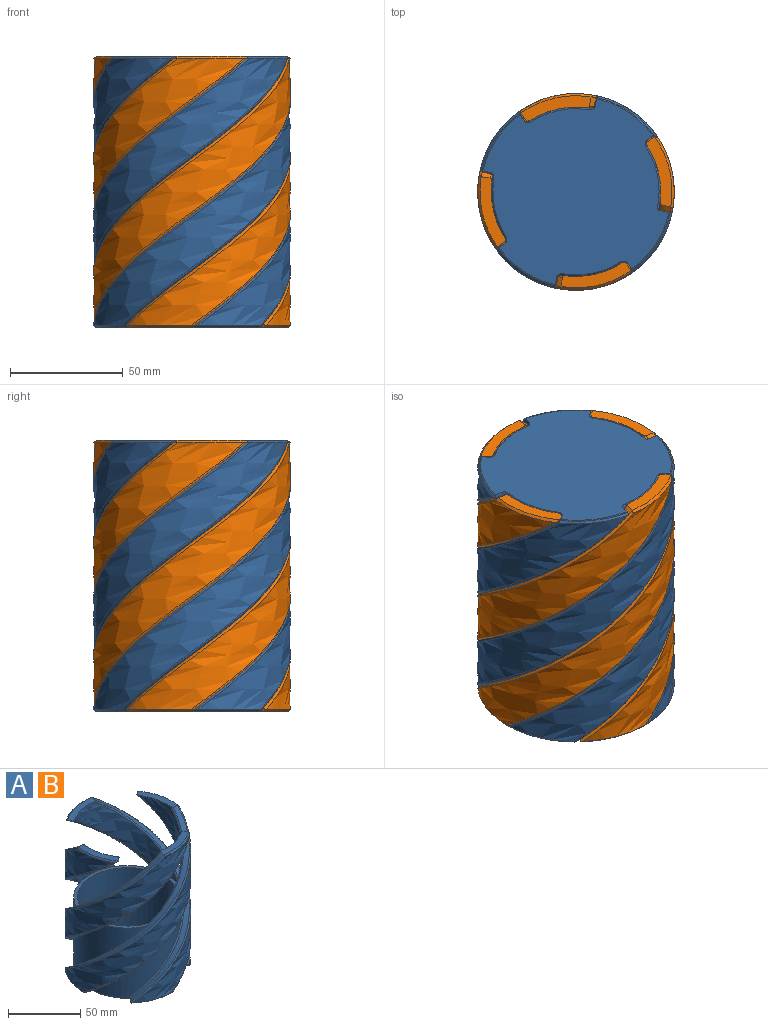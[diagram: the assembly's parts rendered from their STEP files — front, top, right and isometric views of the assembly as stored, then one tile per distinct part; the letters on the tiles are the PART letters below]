
ASSEMBLY  parts=2 mates=1
PART A: 91 faces, bbox 91.5x91.5x134.3 mm
  f0: cylinder r=37.5mm len=70.11mm, axis (0,0,-1), area 1564mm2, adj f4,f53,f57,f67
  f1: cylinder r=37.5mm len=70.11mm, axis (0,0,-1), area 1564mm2, adj f4,f56,f59,f68
  f2: cylinder r=37.5mm len=70.11mm, axis (0,0,-1), area 1564mm2, adj f4,f55,f58,f84
  f3: cylinder r=37.5mm len=70.84mm, axis (0,0,-1), area 1655.3mm2, adj f4,f16,f54,f83,f85
  f4: plane 75.41x75.41mm, normal (0,0,1), area 574.3mm2, adj f0,f1,f2,f3,f6,f10,f15,f16
  f5: plane 84.47x84.47mm, normal (0,0,-1), area 4878.4mm2, adj f62,f63,f64,f65,f66,f67,f68,f69
  f6: cylinder r=35mm len=70mm, axis (0,0,-1), area 11545.4mm2, adj f4,f52
  f7: plane 60x60mm, normal (0,0,1), area 2827.4mm2, adj f52
  f8: plane 32.05x12.18mm, normal (0,0,1), area 156.5mm2, adj f9,f10,f11,f33,f36,f50,f51
  f9: bspline ~130x87mm, area 776mm2, adj f8,f36,f50,f54,f79
  f10: bspline ~80x69.6mm, area 1583mm2, adj f4,f8,f50,f51
  f11: bspline ~130x88.08mm, area 768.6mm2, adj f8,f37,f51,f53,f71
  f12: bspline ~120x91.09mm, area 3627.8mm2, adj f31,f33,f36,f37
  f13: plane 32.05x12.18mm, normal (0,0,1), area 156.4mm2, adj f14,f15,f16,f32,f42,f48,f49
  f14: bspline ~130x87mm, area 776mm2, adj f13,f42,f48,f55,f89
  f15: bspline ~80x69.6mm, area 1583mm2, adj f4,f13,f48,f49
  f16: bspline ~130x88.08mm, area 859.5mm2, adj f3,f4,f13,f43,f49,f85
  f17: bspline ~120x91.09mm, area 3627.8mm2, adj f28,f32,f42,f43
  f18: plane 32.05x12.18mm, normal (0,0,1), area 156.3mm2, adj f20,f21,f22,f35,f41,f46,f47
  f19: bspline ~120x91.09mm, area 3627.8mm2, adj f29,f35,f40,f41
  f20: bspline ~130x87mm, area 776mm2, adj f18,f41,f46,f59,f74
  f21: bspline ~80x69.6mm, area 1583mm2, adj f4,f18,f46,f47
  f22: bspline ~130x88.08mm, area 768.6mm2, adj f18,f40,f47,f58,f80
  f23: plane 32.05x12.18mm, normal (0,0,1), area 157.8mm2, adj f25,f26,f27,f34,f39,f44,f45
  f24: bspline ~120x91.09mm, area 3627.8mm2, adj f30,f34,f38,f39
  f25: bspline ~130x87mm, area 776mm2, adj f23,f39,f44,f57,f63
  f26: bspline ~80x69.6mm, area 1583mm2, adj f4,f23,f44,f45
  f27: bspline ~130x88.08mm, area 768.6mm2, adj f23,f38,f45,f56,f64
  f28: bspline ~32.38x13.54mm, area 35.5mm2, adj f17,f42,f43,f86,f88
  f29: bspline ~32.38x13.54mm, area 35.5mm2, adj f19,f40,f41,f77,f78
  f30: bspline ~32.38x13.54mm, area 35.5mm2, adj f24,f38,f39,f61,f62
  f31: bspline ~32.38x13.54mm, area 35.5mm2, adj f12,f36,f37,f72,f75
  f32: bspline ~35.3x10.09mm, area 45.3mm2, adj f13,f17,f42,f43
  f33: bspline ~35.3x10.09mm, area 45.3mm2, adj f8,f12,f36,f37
  f34: bspline ~35.3x10.09mm, area 45.3mm2, adj f23,f24,f38,f39
  f35: bspline ~35.3x10.09mm, area 45.3mm2, adj f18,f19,f40,f41
  f36: bspline ~121.66x87.02mm, area 315.5mm2, adj f8,f9,f12,f31,f33,f75,f76
  f37: bspline ~120.82x86.66mm, area 314.1mm2, adj f11,f12,f31,f33,f72
  f38: bspline ~120.82x86.66mm, area 314.1mm2, adj f24,f27,f30,f34,f61
  f39: bspline ~121.66x87.02mm, area 315.5mm2, adj f23,f24,f25,f30,f34,f60,f62
  f40: bspline ~120.82x86.66mm, area 314.1mm2, adj f19,f22,f29,f35,f77
  f41: bspline ~121.66x87.02mm, area 315.5mm2, adj f18,f19,f20,f29,f35,f73,f78
  f42: bspline ~121.66x87.02mm, area 315.5mm2, adj f13,f14,f17,f28,f32,f88,f90
  f43: bspline ~120.82x86.66mm, area 314.1mm2, adj f16,f17,f28,f32,f86
  f44: bspline ~64.97x62.2mm, area 145.5mm2, adj f4,f23,f25,f26
  f45: bspline ~64.11x56.76mm, area 145.5mm2, adj f4,f23,f26,f27
  f46: bspline ~64.97x62.2mm, area 145.5mm2, adj f4,f18,f20,f21
  f47: bspline ~64.11x56.76mm, area 145.5mm2, adj f4,f18,f21,f22
  f48: bspline ~64.97x62.2mm, area 145.5mm2, adj f4,f13,f14,f15
  f49: bspline ~64.11x56.76mm, area 145.5mm2, adj f4,f13,f15,f16
  f50: bspline ~64.97x62.2mm, area 145.5mm2, adj f4,f8,f9,f10
  f51: bspline ~64.11x56.76mm, area 145.5mm2, adj f4,f8,f10,f11
  f52: torus R=30mm, axis (0,0,1), area 1637.5mm2, adj f6,f7
  f53: bspline ~64.76x64.57mm, area 143mm2, adj f0,f4,f11,f69
  f54: bspline ~65.62x52.59mm, area 144.4mm2, adj f3,f4,f9,f81
  f55: bspline ~65.62x52.59mm, area 144.4mm2, adj f2,f4,f14,f87
  f56: bspline ~64.76x64.57mm, area 143mm2, adj f1,f4,f27,f66
  f57: bspline ~65.62x52.59mm, area 144.4mm2, adj f0,f4,f25,f65
  f58: bspline ~64.76x64.57mm, area 143mm2, adj f2,f4,f22,f82
  f59: bspline ~65.62x52.59mm, area 144.4mm2, adj f1,f4,f20,f70
  f60: bspline ~0.44x0.16mm, area 0mm2, adj f39,f62,f63
  f61: bspline ~1.3x1.12mm, area 0.7mm2, adj f30,f38,f62,f64
  f62: bspline ~33.37x14.09mm, area 17.3mm2, adj f5,f30,f39,f60,f61,f63,f64
  f63: bspline ~4x0.46mm, area 1.8mm2, adj f5,f25,f60,f62,f65
  f64: bspline ~3.25x3.03mm, area 5.5mm2, adj f5,f27,f61,f62,f66
  f65: bspline ~2.65x1.79mm, area 2.2mm2, adj f5,f57,f63,f67
  f66: bspline ~3.08x1.55mm, area 3.7mm2, adj f5,f56,f64,f68
  f67: cone r=37.5mm half-angle=45deg, axis (0,0,1), area 26.7mm2, adj f0,f5,f65,f69
  f68: cone r=37.5mm half-angle=45deg, axis (0,0,1), area 26.7mm2, adj f1,f5,f66,f70
  f69: bspline ~3.08x1.55mm, area 3.7mm2, adj f5,f53,f67,f71
  f70: bspline ~2.65x1.79mm, area 2.2mm2, adj f5,f59,f68,f74
  f71: bspline ~3.25x3.03mm, area 5.5mm2, adj f5,f11,f69,f72,f75
  f72: bspline ~1.3x1.12mm, area 0.7mm2, adj f31,f37,f71,f75
  f73: bspline ~0.44x0.16mm, area 0mm2, adj f41,f74,f78
  f74: bspline ~4x0.46mm, area 1.8mm2, adj f5,f20,f70,f73,f78
  f75: bspline ~33.37x14.09mm, area 17.3mm2, adj f5,f31,f36,f71,f72,f76,f79
  f76: bspline ~0.44x0.16mm, area 0mm2, adj f36,f75,f79
  f77: bspline ~1.3x1.12mm, area 0.7mm2, adj f29,f40,f78,f80
  f78: bspline ~33.37x14.09mm, area 17.3mm2, adj f5,f29,f41,f73,f74,f77,f80
  f79: bspline ~4x0.46mm, area 1.8mm2, adj f5,f9,f75,f76,f81
  f80: bspline ~3.25x3.03mm, area 5.5mm2, adj f5,f22,f77,f78,f82
  f81: bspline ~2.65x1.79mm, area 2.2mm2, adj f5,f54,f79,f83
  f82: bspline ~3.08x1.55mm, area 3.7mm2, adj f5,f58,f80,f84
  f83: cone r=37.5mm half-angle=45deg, axis (0,0,1), area 29.3mm2, adj f3,f5,f81,f85
  f84: cone r=37.5mm half-angle=45deg, axis (0,0,1), area 26.7mm2, adj f2,f5,f82,f87
  f85: bspline ~4.53x4.2mm, area 7.1mm2, adj f3,f5,f16,f83,f86,f88
  f86: bspline ~1.3x1.12mm, area 0.7mm2, adj f28,f43,f85,f88
  f87: bspline ~2.65x1.79mm, area 2.2mm2, adj f5,f55,f84,f89
  f88: bspline ~33.37x14.09mm, area 17.3mm2, adj f5,f28,f42,f85,f86,f89,f90
  f89: bspline ~4x0.46mm, area 1.8mm2, adj f5,f14,f87,f88,f90
  f90: bspline ~0.44x0.16mm, area 0mm2, adj f42,f88,f89
PART B: same geometry as A
PLACE A rot(axis=(-0.46,-0.89,0),180deg) t=(0,0,120)mm
PLACE B at identity fixed
MATE cylindrical A.f0 <-> B.f0  axis (0,0,-1) through (0,0,60)mm
